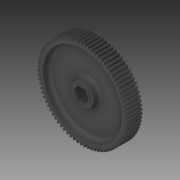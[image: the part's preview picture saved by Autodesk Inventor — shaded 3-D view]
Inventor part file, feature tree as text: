
AUTODESK INVENTOR PART (.ipt)
format: ipt  version: 2019 (Build 230136000, 136)  size: 773,120 bytes
history: native  units: in
note: dims shown in document units (in); Inventor stores cm internally (conversion verified against a paired STEP export)
features: mirror x1
ambient origin geometry x8: Origin, YZ Plane, XZ Plane, XY Plane, X Axis, Y Axis, Z Axis, Center Point
bodies: Solid1 (feature_tree)
feature tree (1):
  mirror  "Mirror1"
